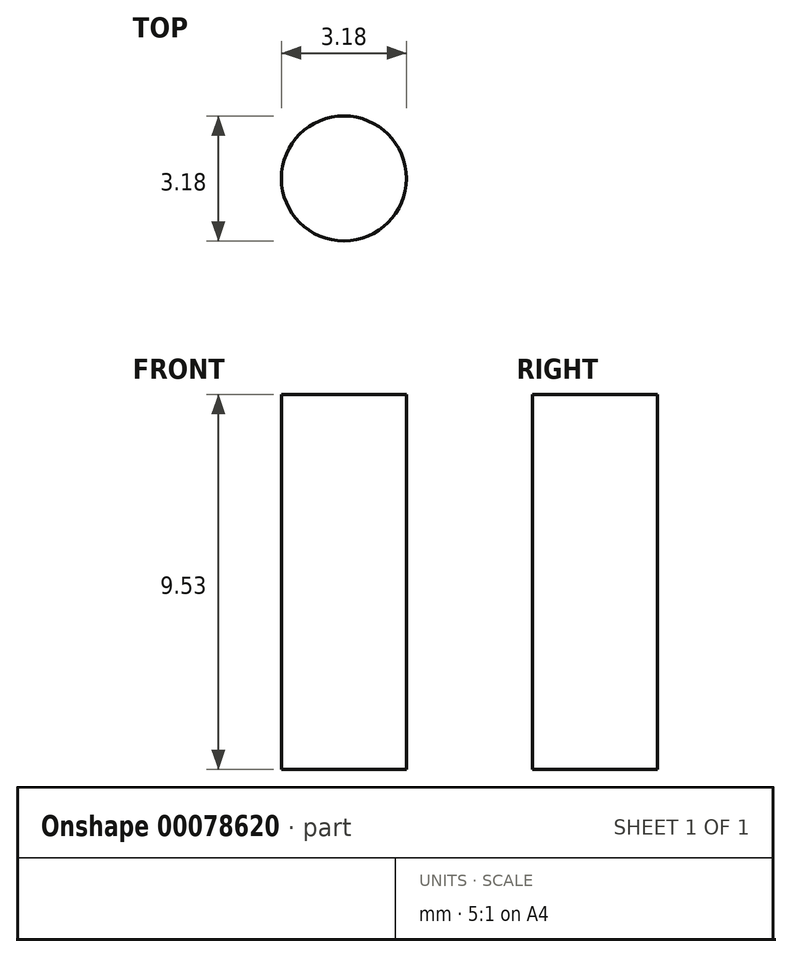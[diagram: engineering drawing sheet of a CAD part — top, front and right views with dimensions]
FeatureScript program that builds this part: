
annotation { "Feature Type Name" : "Feature", "Feature Type Description" : "" }
export const myFeature = defineFeature(function(context is Context, id is Id, definition is map)
    precondition{}
    {
        {
            var Q0;
            Q0=qCreatedBy(makeId("Top.planeOp"),FACE);
            var sketch = newSketch(context, id + "F0", { "sketchPlane" : qUnion([Q0])});
            skCircle(sketch, "E0", {"center": v(0, 0) * mm, "radius": 1.59 * mm});
            skSolve(sketch);
        }
        {
            var Q0;
            Q0 = qSketchRegion(id + "F0", true);
            extrude(context, id + "F1", {"entities" : qUnion([Q0]), "depth" : 9.52 * mm});
        }
    });
